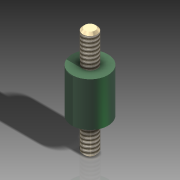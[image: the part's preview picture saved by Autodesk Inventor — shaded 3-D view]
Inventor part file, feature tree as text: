
AUTODESK INVENTOR PART (.ipt)
format: ipt  version: 2011 (Build 150239000, 239)  size: 99,328 bytes
history: native  units: in
note: dims shown in document units (in); Inventor stores cm internally (conversion verified against a paired STEP export)
features: thread x2, other x1, imported_body x1
ambient origin geometry x8: Origin, YZ Plane, XZ Plane, XY Plane, X Axis, Y Axis, Z Axis, Center Point
feature tree (4):
  parser-record x1  (decoder bookkeeping rows leaked as tree rows — omitted from the tree; the rows remain in map.json)
  imported_body  "Base1"
  thread  "Thread1"  [1 undecoded]
  thread  "Thread2"  [1 undecoded]
note: 2 required parameter values undecoded (feature->parameter linkage not recoverable at this tier; creation-order binding heuristic only, values carry confidence <= 0.55)
